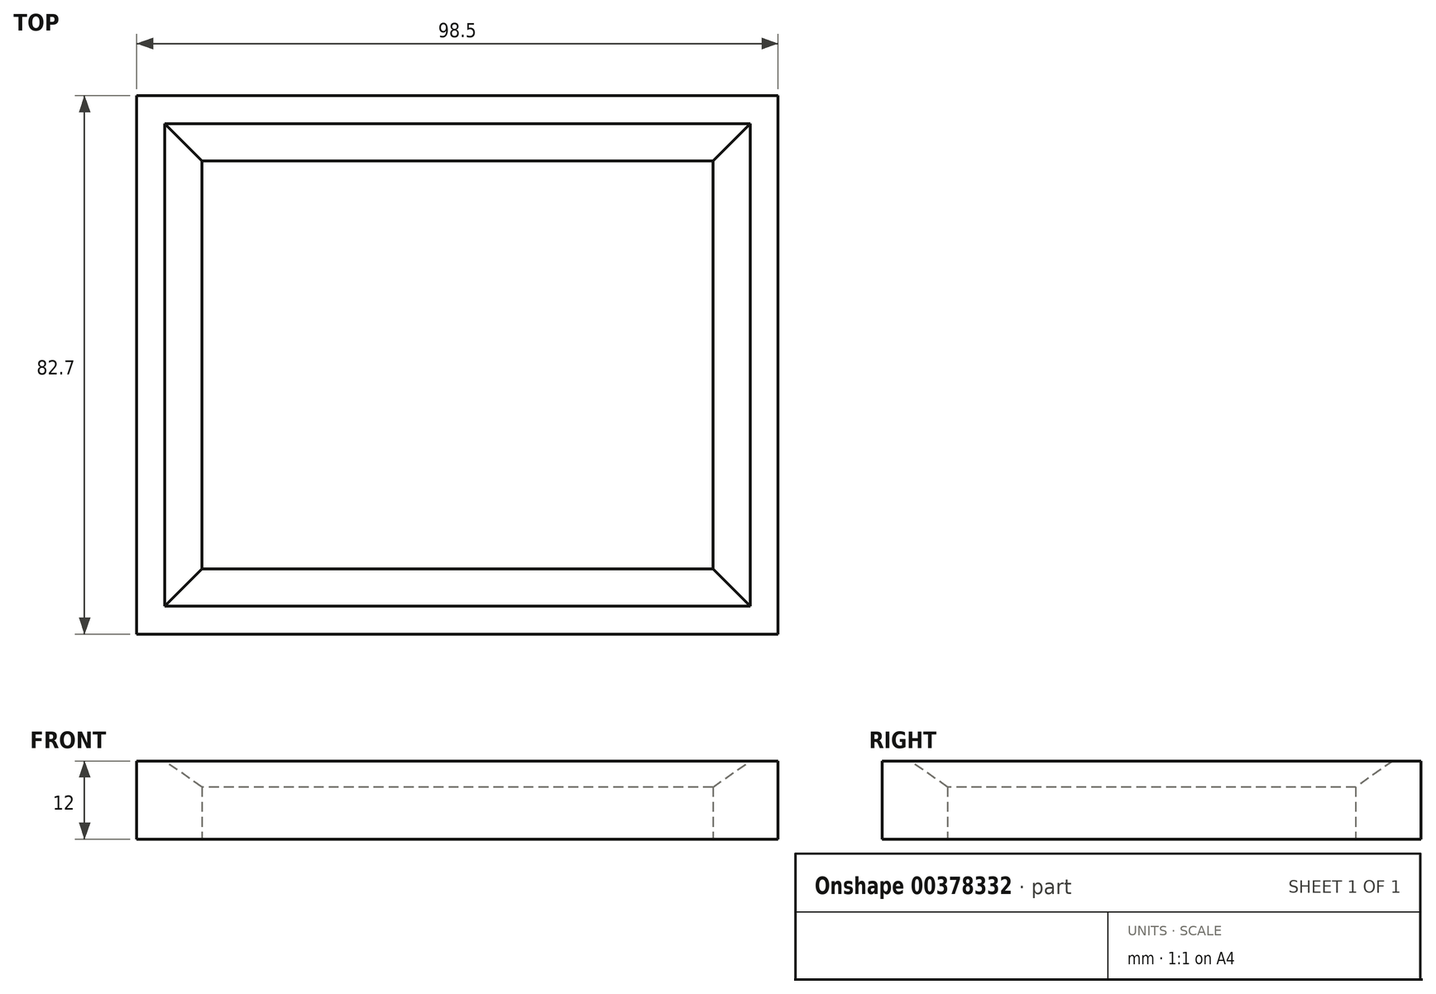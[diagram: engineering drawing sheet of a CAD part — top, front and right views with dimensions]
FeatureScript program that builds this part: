
annotation { "Feature Type Name" : "Feature", "Feature Type Description" : "" }
export const myFeature = defineFeature(function(context is Context, id is Id, definition is map)
    precondition{}
    {
        {
            var Q0;
            Q0=qCreatedBy(makeId("Top.planeOp"),FACE);
            var sketch = newSketch(context, id + "F0", { "sketchPlane" : qUnion([Q0])});
            skLineSegment(sketch, "E0.bottom", {"start": v(0, 0) * mm, "end": v(78.5, 0) * mm});
            skLineSegment(sketch, "E0.top", {"start": v(0, -62.7) * mm, "end": v(78.5, -62.7) * mm});
            skLineSegment(sketch, "E0.left", {"start": v(0, 0) * mm, "end": v(0, -62.7) * mm});
            skLineSegment(sketch, "E0.right", {"start": v(78.5, 0) * mm, "end": v(78.5, -62.7) * mm});
            skLineSegment(sketch, "E1.bottom", {"start": v(-10, 10) * mm, "end": v(88.5, 10) * mm});
            skLineSegment(sketch, "E1.top", {"start": v(-10, -72.7) * mm, "end": v(88.5, -72.7) * mm});
            skLineSegment(sketch, "E1.left", {"start": v(-10, 10) * mm, "end": v(-10, -72.7) * mm});
            skLineSegment(sketch, "E1.right", {"start": v(88.5, 10) * mm, "end": v(88.5, -72.7) * mm});
            skSolve(sketch);
        }
        {
            var Q0;
            Q0=makeQuery(id+"F0.imprint","IMPRINT",FACE,{"disambiguationData":[TD([[makeQuery(id+"F0.imprint","IMPRINT",EDGE,{"derivedFrom":sQuery(id+"F0.wireOp",EDGE,"E0.bottom")}),1.0]])]});
            extrude(context, id + "F1", {"entities" : qUnion([Q0]), "depth" : 12 * mm});
        }
        {
            var Q0;
            Q0=makeQuery(id+"F1.opExtrude","CAP_EDGE",EDGE,{"disambiguationData":[OSD([sQuery(id+"F0.wireOp",EDGE,"E0.top")])],"isStart":false});
            var Q1;
            Q1=makeQuery(id+"F1.opExtrude","CAP_EDGE",EDGE,{"disambiguationData":[OSD([sQuery(id+"F0.wireOp",EDGE,"E0.right")])],"isStart":false});
            var Q2;
            Q2=makeQuery(id+"F1.opExtrude","CAP_EDGE",EDGE,{"disambiguationData":[OSD([sQuery(id+"F0.wireOp",EDGE,"E0.bottom")])],"isStart":false});
            var Q3;
            Q3=makeQuery(id+"F1.opExtrude","CAP_EDGE",EDGE,{"disambiguationData":[OSD([sQuery(id+"F0.wireOp",EDGE,"E0.left")])],"isStart":false});
            chamfer(context, id + "F2", {"entities" : qUnion([Q0, Q1, Q2, Q3]), "chamferType" : ChamferType.OFFSET_ANGLE, "width" : 4 * mm, "oppositeDirection" : false, "angle" : 55 * degree, "tangentPropagation" : true});
        }
    });
